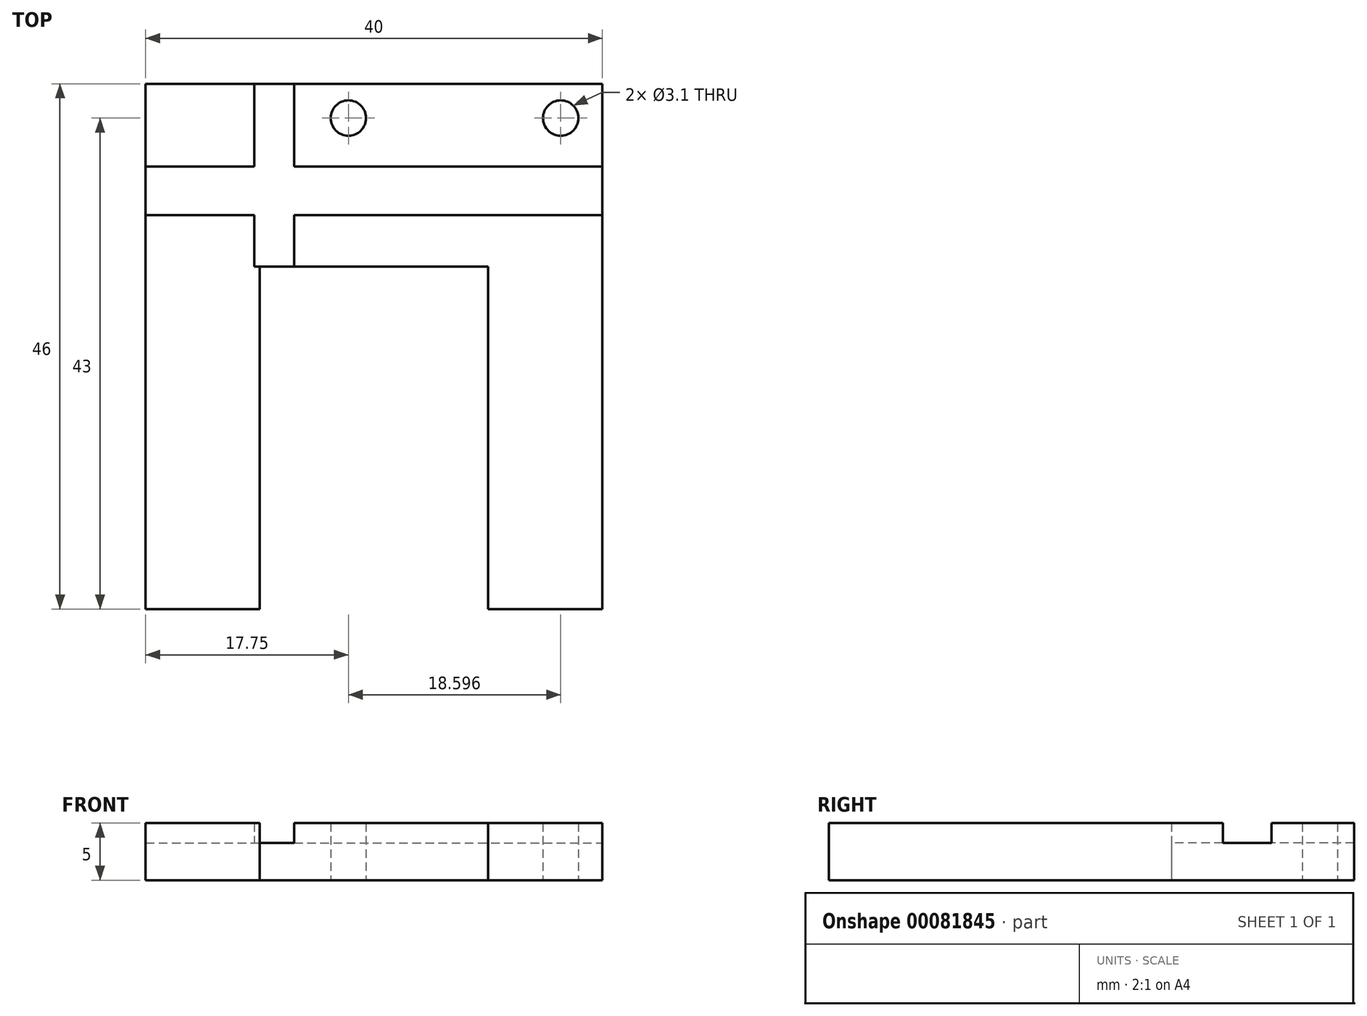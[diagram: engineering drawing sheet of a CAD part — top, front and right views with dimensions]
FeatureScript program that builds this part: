
annotation { "Feature Type Name" : "Feature", "Feature Type Description" : "" }
export const myFeature = defineFeature(function(context is Context, id is Id, definition is map)
    precondition{}
    {
        {
            var Q0;
            Q0=qCreatedBy(makeId("Top.planeOp"),FACE);
            var sketch = newSketch(context, id + "F0", { "sketchPlane" : qUnion([Q0])});
            skLineSegment(sketch, "E0", {"start": v(-20, -30) * mm, "end": v(-20, 0) * mm, "construction": true});
            skLineSegment(sketch, "E1", {"start": v(-20, 16) * mm, "end": v(-10.5, 16) * mm, "construction": true});
            skLineSegment(sketch, "E2", {"start": v(20, 16) * mm, "end": v(20, 13) * mm, "construction": true});
            skLineSegment(sketch, "E3", {"start": v(20, -30) * mm, "end": v(10, -30) * mm, "construction": true});
            skLineSegment(sketch, "E4", {"start": v(10, -30) * mm, "end": v(10, 0) * mm, "construction": true});
            skLineSegment(sketch, "E5", {"start": v(20, 0) * mm, "end": v(-20, 0) * mm, "construction": true});
            skLineSegment(sketch, "E6", {"start": v(-10, 0) * mm, "end": v(-10, -30) * mm, "construction": true});
            skLineSegment(sketch, "E7", {"start": v(-10, -30) * mm, "end": v(-20, -30) * mm, "construction": true});
            skLineSegment(sketch, "E8", {"start": v(-20, 0) * mm, "end": v(-20, 16) * mm, "construction": true});
            skLineSegment(sketch, "E9", {"start": v(20, 13) * mm, "end": v(-20, 13) * mm, "construction": true});
            skLineSegment(sketch, "E10", {"start": v(20, 4.5) * mm, "end": v(-20, 4.5) * mm, "construction": true});
            skLineSegment(sketch, "E11", {"start": v(20, 8.75) * mm, "end": v(-20, 8.75) * mm, "construction": true});
            skLineSegment(sketch, "E12", {"start": v(-10.5, 16) * mm, "end": v(-10.5, 0) * mm, "construction": true});
            skLineSegment(sketch, "E13", {"start": v(-7, 16) * mm, "end": v(-7, 0) * mm, "construction": true});
            skLineSegment(sketch, "E14", {"start": v(16.35, 16) * mm, "end": v(16.35, 0) * mm, "construction": true});
            skLineSegment(sketch, "E15", {"start": v(-2.25, 16) * mm, "end": v(-2.25, 0) * mm, "construction": true});
            skLineSegment(sketch, "E16", {"start": v(16.75, 16) * mm, "end": v(20, 16) * mm, "construction": true});
            skLineSegment(sketch, "E17", {"start": v(-2.25, 16) * mm, "end": v(16.75, 16) * mm, "construction": true});
            skLineSegment(sketch, "E18", {"start": v(-7, 16) * mm, "end": v(-2.25, 16) * mm, "construction": true});
            skLineSegment(sketch, "E19", {"start": v(-10.5, 16) * mm, "end": v(-7, 16) * mm, "construction": true});
            skPoint(sketch, "E20", {"position": v(0, 0) * mm});
            skLineSegment(sketch, "E21", {"start": v(20, 13) * mm, "end": v(20, 8.75) * mm, "construction": true});
            skLineSegment(sketch, "E22", {"start": v(20, 8.75) * mm, "end": v(20, 4.5) * mm, "construction": true});
            skLineSegment(sketch, "E23", {"start": v(20, 4.5) * mm, "end": v(20, 0) * mm, "construction": true});
            skLineSegment(sketch, "E24", {"start": v(20, 0) * mm, "end": v(20, -30) * mm, "construction": true});
            skLineSegment(sketch, "E25", {"start": v(-20, 16) * mm, "end": v(-20, -30) * mm});
            skLineSegment(sketch, "E26", {"start": v(-10, -30) * mm, "end": v(-20, -30) * mm});
            skLineSegment(sketch, "E27", {"start": v(-10, -30) * mm, "end": v(-10, 0) * mm});
            skLineSegment(sketch, "E28", {"start": v(-10, 0) * mm, "end": v(10, 0) * mm});
            skLineSegment(sketch, "E29", {"start": v(10, 0) * mm, "end": v(10, -30) * mm});
            skLineSegment(sketch, "E30", {"start": v(10, -30) * mm, "end": v(20, -30) * mm});
            skLineSegment(sketch, "E31", {"start": v(20, -30) * mm, "end": v(20, 16) * mm});
            skLineSegment(sketch, "E32", {"start": v(20, 16) * mm, "end": v(-20, 16) * mm});
            skLineSegment(sketch, "E33", {"start": v(-10.5, 0) * mm, "end": v(-7, 0) * mm});
            skLineSegment(sketch, "E34", {"start": v(-7, 0) * mm, "end": v(-7, 4.5) * mm});
            skLineSegment(sketch, "E35", {"start": v(-7, 4.5) * mm, "end": v(20, 4.5) * mm});
            skLineSegment(sketch, "E36", {"start": v(20, 4.5) * mm, "end": v(20, 8.75) * mm});
            skLineSegment(sketch, "E37", {"start": v(20, 8.75) * mm, "end": v(-7, 8.75) * mm});
            skLineSegment(sketch, "E38", {"start": v(-7, 8.75) * mm, "end": v(-7, 16) * mm});
            skLineSegment(sketch, "E39", {"start": v(-7, 16) * mm, "end": v(-10.5, 16) * mm});
            skLineSegment(sketch, "E40", {"start": v(-10.5, 16) * mm, "end": v(-10.5, 8.75) * mm});
            skLineSegment(sketch, "E41", {"start": v(-10.5, 8.75) * mm, "end": v(-20, 8.75) * mm});
            skLineSegment(sketch, "E42", {"start": v(-20, 8.75) * mm, "end": v(-20, 4.5) * mm});
            skLineSegment(sketch, "E43", {"start": v(-20, 4.5) * mm, "end": v(-10.5, 4.5) * mm});
            skLineSegment(sketch, "E44", {"start": v(-10.5, 4.5) * mm, "end": v(-10.5, 0) * mm});
            skCircle(sketch, "E45", {"center": v(-2.25, 13) * mm, "radius": 1.55 * mm});
            skCircle(sketch, "E46", {"center": v(16.35, 13) * mm, "radius": 1.55 * mm});
            skSolve(sketch);
        }
        {
            var Q0;
            {var subQ3=sQuery(id+"F0.wireOp",EDGE,"E26");Q0=makeQuery(id+"F0.imprint","IMPRINT",FACE,{"disambiguationData":[TD([[makeQuery(id+"F0.imprint","IMPRINT",EDGE,{"derivedFrom":subQ3}),-1.0]])]});}
            var Q1;
            {var subQ4=sQuery(id+"F0.wireOp",EDGE,"E40");Q1=makeQuery(id+"F0.imprint","IMPRINT",FACE,{"disambiguationData":[TD([[makeQuery(id+"F0.imprint","IMPRINT",EDGE,{"derivedFrom":subQ4}),-1.0]])]});}
            var Q2;
            {var subQ1=sQuery(id+"F0.wireOp",EDGE,"E37");Q2=makeQuery(id+"F0.imprint","IMPRINT",FACE,{"disambiguationData":[TD([[makeQuery(id+"F0.imprint","IMPRINT",EDGE,{"derivedFrom":subQ1}),-1.0]])]});}
            var Q3;
            Q3=makeQuery(id+"F0.imprint","IMPRINT",FACE,{"disambiguationData":[TD([[makeQuery(id+"F0.imprint","IMPRINT",EDGE,{"derivedFrom":sQuery(id+"F0.wireOp",EDGE,"E28")}),1.0]])]});
            extrude(context, id + "F1", {"entities" : qUnion([Q0, Q1, Q2, Q3]), "depth" : 5 * mm});
        }
        {
            var Q0;
            {var subQ0=sQuery(id+"F0.wireOp",EDGE,"E34");Q0=makeQuery(id+"F0.imprint","IMPRINT",FACE,{"disambiguationData":[TD([[makeQuery(id+"F0.imprint","IMPRINT",EDGE,{"derivedFrom":subQ0}),1.0]])]});}
            extrude(context, id + "F2", {"entities" : qUnion([Q0]), "operationType" : NewBodyOperationType.ADD, "depth" : 3.25 * mm});
        }
    });
